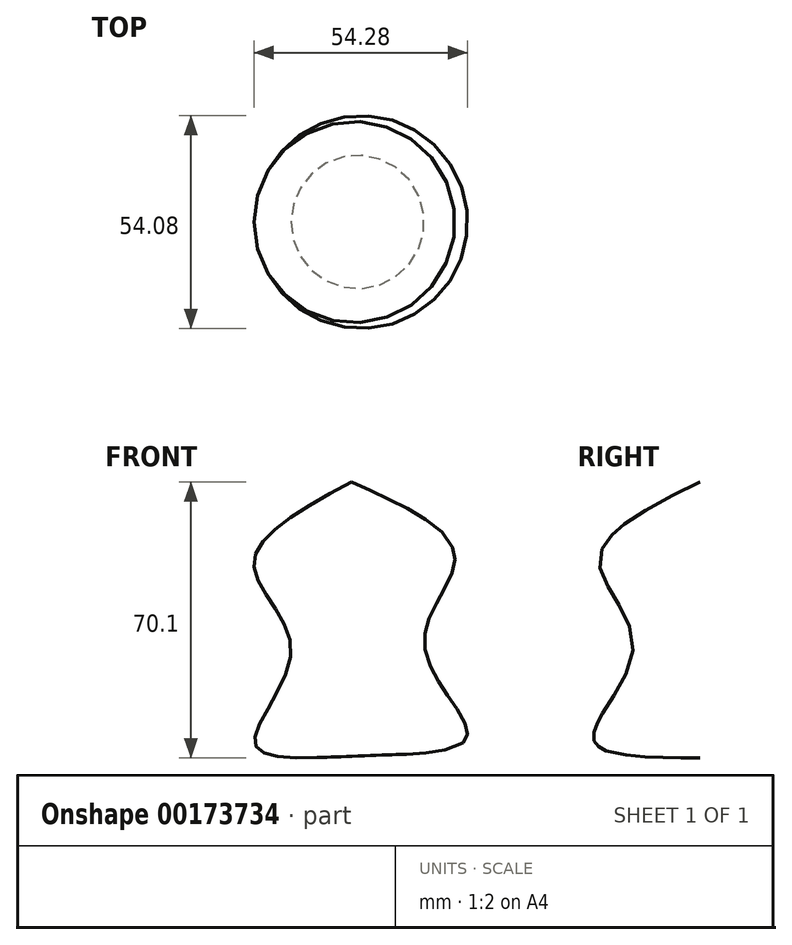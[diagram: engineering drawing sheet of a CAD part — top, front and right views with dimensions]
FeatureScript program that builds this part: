
annotation { "Feature Type Name" : "Feature", "Feature Type Description" : "" }
export const myFeature = defineFeature(function(context is Context, id is Id, definition is map)
    precondition{}
    {
        {
            var Q0;
            Q0=qCreatedBy(makeId("Front.planeOp"),FACE);
            var sketch = newSketch(context, id + "F0", { "sketchPlane" : qUnion([Q0])});
            skFitSpline(sketch, "E0", {"points": [v(-15.38, 45.49) * mm, v(-40.15, 24.55) * mm, v(-30.72, 2.73) * mm, v(-39.86, -20.87) * mm, v(-12.73, -23.81) * mm], "startDerivative": vector(-136.69, -73.71) * mm, "endDerivative": vector(155.93, 11.72) * mm});
            skLineSegment(sketch, "E1", {"start": v(-15.38, 45.49) * mm, "end": v(-12.73, -23.81) * mm});
            skSolve(sketch);
        }
        {
            var Q0;
            Q0=makeQuery(id+"F0.imprint","IMPRINT",FACE,{"disambiguationData":[TD([[makeQuery(id+"F0.imprint","IMPRINT",EDGE,{"derivedFrom":sQuery(id+"F0.wireOp",EDGE,"E0")}),1.0]])]});
            var Q1;
            Q1=sQuery(id+"F0.wireOp",EDGE,"E1");
            revolve(context, id + "F1", {"entities" : qUnion([Q0]), "axis" : qUnion([Q1]), "revolveType" : RevolveType.FULL, "oppositeDirection" : true});
        }
    });
